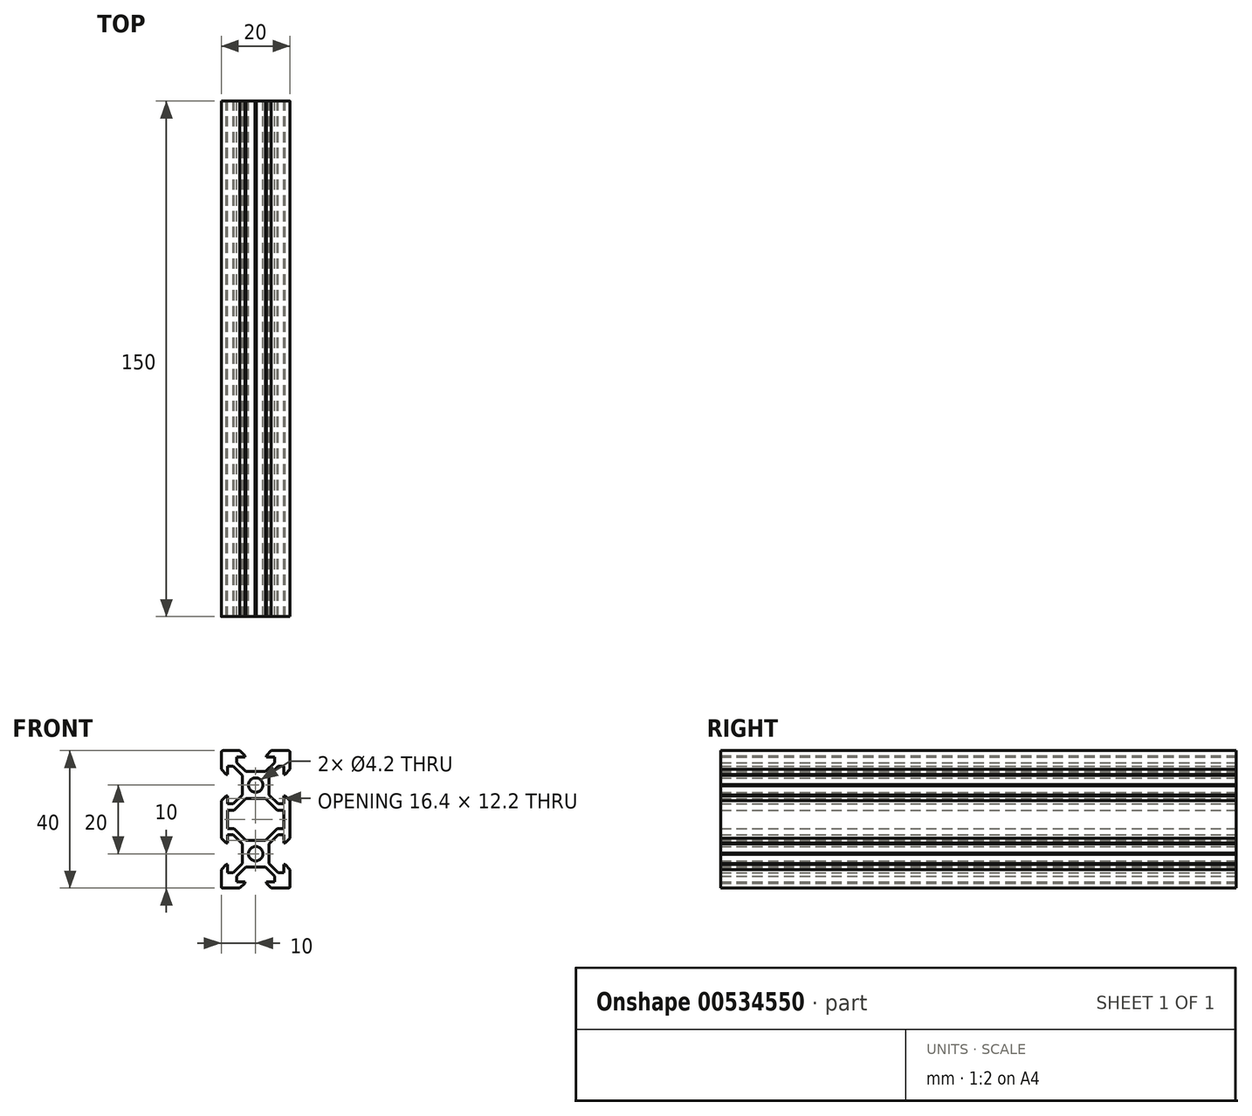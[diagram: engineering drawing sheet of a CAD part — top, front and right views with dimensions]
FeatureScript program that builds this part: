
annotation { "Feature Type Name" : "Feature", "Feature Type Description" : "" }
export const myFeature = defineFeature(function(context is Context, id is Id, definition is map)
    precondition{}
    {
        {
            var Q0;
            Q0=qCreatedBy(makeId("Front.planeOp"),FACE);
            var sketch = newSketch(context, id + "F0", { "sketchPlane" : qUnion([Q0])});
            skLineSegment(sketch, "E0.0.0", {"start": v(-3.69, 10) * mm, "end": v(-3.9, 9.79) * mm});
            skLineSegment(sketch, "E0.0.1", {"start": v(-3.9, 9.8) * mm, "end": v(-3.9, 7.16) * mm});
            skLineSegment(sketch, "E0.0.2", {"start": v(-3.9, 7.16) * mm, "end": v(-6.56, 4.5) * mm});
            skLineSegment(sketch, "E0.0.3", {"start": v(-6.56, 4.5) * mm, "end": v(-8.2, 4.5) * mm});
            skLineSegment(sketch, "E0.0.4", {"start": v(-8.2, 4.5) * mm, "end": v(-8.2, 6.88) * mm});
            skLineSegment(sketch, "E0.0.5", {"start": v(-8.2, 6.87) * mm, "end": v(-8.54, 6.87) * mm});
            skLineSegment(sketch, "E0.0.6", {"start": v(-8.54, 6.87) * mm, "end": v(-10, 5.42) * mm});
            skLineSegment(sketch, "E0.0.7", {"start": v(-10, 5.42) * mm, "end": v(-10, -5.42) * mm});
            skLineSegment(sketch, "E0.0.8", {"start": v(-10, -5.42) * mm, "end": v(-8.54, -6.87) * mm});
            skLineSegment(sketch, "E0.0.9", {"start": v(-8.54, -6.88) * mm, "end": v(-8.2, -6.88) * mm});
            skLineSegment(sketch, "E0.0.10", {"start": v(-8.2, -6.87) * mm, "end": v(-8.2, -4.5) * mm});
            skLineSegment(sketch, "E0.0.11", {"start": v(-8.2, -4.5) * mm, "end": v(-6.56, -4.5) * mm});
            skLineSegment(sketch, "E0.0.12", {"start": v(-6.56, -4.5) * mm, "end": v(-3.9, -7.16) * mm});
            skLineSegment(sketch, "E0.0.13", {"start": v(-3.9, -7.16) * mm, "end": v(-3.9, -9.79) * mm});
            skLineSegment(sketch, "E0.0.14", {"start": v(-3.9, -9.79) * mm, "end": v(-3.69, -10) * mm});
            skLineSegment(sketch, "E0.0.15", {"start": v(-3.69, -10) * mm, "end": v(-3.9, -10.21) * mm});
            skLineSegment(sketch, "E0.0.16", {"start": v(-3.9, -10.2) * mm, "end": v(-3.9, -12.84) * mm});
            skLineSegment(sketch, "E0.0.17", {"start": v(-3.9, -12.84) * mm, "end": v(-6.56, -15.5) * mm});
            skLineSegment(sketch, "E0.0.18", {"start": v(-6.56, -15.5) * mm, "end": v(-8.2, -15.5) * mm});
            skLineSegment(sketch, "E0.0.19", {"start": v(-8.2, -15.5) * mm, "end": v(-8.2, -13.12) * mm});
            skLineSegment(sketch, "E0.0.20", {"start": v(-8.2, -13.13) * mm, "end": v(-8.54, -13.13) * mm});
            skLineSegment(sketch, "E0.0.21", {"start": v(-8.54, -13.12) * mm, "end": v(-10, -14.58) * mm});
            skLineSegment(sketch, "E0.0.22", {"start": v(-10, -14.58) * mm, "end": v(-10, -19.5) * mm});
            skArc(sketch, "E0.0.23", {"start": v(-10, -19.5) * mm, "mid": v(-9.85, -19.85) * mm, "end": v(-9.5, -20) * mm});
            skLineSegment(sketch, "E0.0.24", {"start": v(-9.5, -20) * mm, "end": v(-4.58, -20) * mm});
            skLineSegment(sketch, "E0.0.25", {"start": v(-4.58, -20) * mm, "end": v(-3.13, -18.55) * mm});
            skLineSegment(sketch, "E0.0.26", {"start": v(-3.13, -18.54) * mm, "end": v(-3.13, -18.2) * mm});
            skLineSegment(sketch, "E0.0.27", {"start": v(-3.13, -18.2) * mm, "end": v(-5.5, -18.2) * mm});
            skLineSegment(sketch, "E0.0.28", {"start": v(-5.5, -18.2) * mm, "end": v(-5.5, -16.56) * mm});
            skLineSegment(sketch, "E0.0.29", {"start": v(-5.5, -16.56) * mm, "end": v(-2.84, -13.9) * mm});
            skLineSegment(sketch, "E0.0.30", {"start": v(-2.84, -13.9) * mm, "end": v(-0.21, -13.9) * mm});
            skLineSegment(sketch, "E0.0.31", {"start": v(-0.21, -13.9) * mm, "end": v(0, -13.7) * mm});
            skLineSegment(sketch, "E0.0.32", {"start": v(0, -13.69) * mm, "end": v(0.2, -13.9) * mm});
            skLineSegment(sketch, "E0.0.33", {"start": v(0.2, -13.9) * mm, "end": v(2.84, -13.9) * mm});
            skLineSegment(sketch, "E0.0.34", {"start": v(2.84, -13.9) * mm, "end": v(5.5, -16.56) * mm});
            skLineSegment(sketch, "E0.0.35", {"start": v(5.5, -16.56) * mm, "end": v(5.5, -18.2) * mm});
            skLineSegment(sketch, "E0.0.36", {"start": v(5.5, -18.2) * mm, "end": v(3.12, -18.2) * mm});
            skLineSegment(sketch, "E0.0.37", {"start": v(3.12, -18.2) * mm, "end": v(3.12, -18.54) * mm});
            skLineSegment(sketch, "E0.0.38", {"start": v(3.12, -18.54) * mm, "end": v(4.58, -20) * mm});
            skLineSegment(sketch, "E0.0.39", {"start": v(4.58, -20) * mm, "end": v(9.5, -20) * mm});
            skArc(sketch, "E0.0.40", {"start": v(9.5, -20) * mm, "mid": v(9.85, -19.85) * mm, "end": v(10, -19.5) * mm});
            skLineSegment(sketch, "E0.0.41", {"start": v(10, -19.5) * mm, "end": v(10, -14.58) * mm});
            skLineSegment(sketch, "E0.0.42", {"start": v(10, -14.58) * mm, "end": v(8.54, -13.12) * mm});
            skLineSegment(sketch, "E0.0.43", {"start": v(8.55, -13.13) * mm, "end": v(8.2, -13.13) * mm});
            skLineSegment(sketch, "E0.0.44", {"start": v(8.2, -13.12) * mm, "end": v(8.2, -15.5) * mm});
            skLineSegment(sketch, "E0.0.45", {"start": v(8.2, -15.5) * mm, "end": v(6.56, -15.5) * mm});
            skLineSegment(sketch, "E0.0.46", {"start": v(6.56, -15.5) * mm, "end": v(3.9, -12.84) * mm});
            skLineSegment(sketch, "E0.0.47", {"start": v(3.9, -12.84) * mm, "end": v(3.9, -10.2) * mm});
            skLineSegment(sketch, "E0.0.48", {"start": v(3.9, -10.21) * mm, "end": v(3.69, -10) * mm});
            skLineSegment(sketch, "E0.0.49", {"start": v(3.7, -10) * mm, "end": v(3.9, -9.79) * mm});
            skLineSegment(sketch, "E0.0.50", {"start": v(3.9, -9.79) * mm, "end": v(3.9, -7.16) * mm});
            skLineSegment(sketch, "E0.0.51", {"start": v(3.9, -7.16) * mm, "end": v(6.56, -4.5) * mm});
            skLineSegment(sketch, "E0.0.52", {"start": v(6.56, -4.5) * mm, "end": v(8.2, -4.5) * mm});
            skLineSegment(sketch, "E0.0.53", {"start": v(8.2, -4.5) * mm, "end": v(8.2, -6.87) * mm});
            skLineSegment(sketch, "E0.0.54", {"start": v(8.2, -6.88) * mm, "end": v(8.55, -6.88) * mm});
            skLineSegment(sketch, "E0.0.55", {"start": v(8.55, -6.87) * mm, "end": v(10, -5.42) * mm});
            skLineSegment(sketch, "E0.0.56", {"start": v(10, -5.42) * mm, "end": v(10, 5.42) * mm});
            skLineSegment(sketch, "E0.0.57", {"start": v(10, 5.42) * mm, "end": v(8.55, 6.87) * mm});
            skLineSegment(sketch, "E0.0.58", {"start": v(8.55, 6.87) * mm, "end": v(8.2, 6.87) * mm});
            skLineSegment(sketch, "E0.0.59", {"start": v(8.2, 6.88) * mm, "end": v(8.2, 4.5) * mm});
            skLineSegment(sketch, "E0.0.60", {"start": v(8.2, 4.5) * mm, "end": v(6.56, 4.5) * mm});
            skLineSegment(sketch, "E0.0.61", {"start": v(6.56, 4.5) * mm, "end": v(3.9, 7.16) * mm});
            skLineSegment(sketch, "E0.0.62", {"start": v(3.9, 7.16) * mm, "end": v(3.9, 9.8) * mm});
            skLineSegment(sketch, "E0.0.63", {"start": v(3.9, 9.79) * mm, "end": v(3.69, 10) * mm});
            skLineSegment(sketch, "E0.0.64", {"start": v(3.7, 10) * mm, "end": v(3.9, 10.2) * mm});
            skLineSegment(sketch, "E0.0.65", {"start": v(3.9, 10.21) * mm, "end": v(3.9, 12.84) * mm});
            skLineSegment(sketch, "E0.0.66", {"start": v(3.9, 12.84) * mm, "end": v(6.56, 15.5) * mm});
            skLineSegment(sketch, "E0.0.67", {"start": v(6.56, 15.5) * mm, "end": v(8.2, 15.5) * mm});
            skLineSegment(sketch, "E0.0.68", {"start": v(8.2, 15.5) * mm, "end": v(8.2, 13.13) * mm});
            skLineSegment(sketch, "E0.0.69", {"start": v(8.2, 13.12) * mm, "end": v(8.55, 13.12) * mm});
            skLineSegment(sketch, "E0.0.70", {"start": v(8.55, 13.12) * mm, "end": v(10, 14.58) * mm});
            skLineSegment(sketch, "E0.0.71", {"start": v(10, 14.58) * mm, "end": v(10, 19.5) * mm});
            skArc(sketch, "E0.0.72", {"start": v(10, 19.5) * mm, "mid": v(9.85, 19.85) * mm, "end": v(9.5, 20) * mm});
            skLineSegment(sketch, "E0.0.73", {"start": v(9.5, 20) * mm, "end": v(4.58, 20) * mm});
            skLineSegment(sketch, "E0.0.74", {"start": v(4.58, 20) * mm, "end": v(3.13, 18.55) * mm});
            skLineSegment(sketch, "E0.0.75", {"start": v(3.13, 18.55) * mm, "end": v(3.13, 18.2) * mm});
            skLineSegment(sketch, "E0.0.76", {"start": v(3.13, 18.2) * mm, "end": v(5.5, 18.2) * mm});
            skLineSegment(sketch, "E0.0.77", {"start": v(5.5, 18.2) * mm, "end": v(5.5, 16.56) * mm});
            skLineSegment(sketch, "E0.0.78", {"start": v(5.5, 16.56) * mm, "end": v(2.84, 13.9) * mm});
            skLineSegment(sketch, "E0.0.79", {"start": v(2.84, 13.9) * mm, "end": v(0.21, 13.9) * mm});
            skLineSegment(sketch, "E0.0.80", {"start": v(0.21, 13.9) * mm, "end": v(0, 13.7) * mm});
            skLineSegment(sketch, "E0.0.81", {"start": v(0, 13.7) * mm, "end": v(-0.21, 13.9) * mm});
            skLineSegment(sketch, "E0.0.82", {"start": v(-0.2, 13.9) * mm, "end": v(-2.84, 13.9) * mm});
            skLineSegment(sketch, "E0.0.83", {"start": v(-2.84, 13.9) * mm, "end": v(-5.5, 16.56) * mm});
            skLineSegment(sketch, "E0.0.84", {"start": v(-5.5, 16.56) * mm, "end": v(-5.5, 18.2) * mm});
            skLineSegment(sketch, "E0.0.85", {"start": v(-5.5, 18.2) * mm, "end": v(-3.12, 18.2) * mm});
            skLineSegment(sketch, "E0.0.86", {"start": v(-3.12, 18.2) * mm, "end": v(-3.12, 18.55) * mm});
            skLineSegment(sketch, "E0.0.87", {"start": v(-3.12, 18.55) * mm, "end": v(-4.58, 20) * mm});
            skLineSegment(sketch, "E0.0.88", {"start": v(-4.58, 20) * mm, "end": v(-9.5, 20) * mm});
            skArc(sketch, "E0.0.89", {"start": v(-9.5, 20) * mm, "mid": v(-9.85, 19.85) * mm, "end": v(-10, 19.5) * mm});
            skLineSegment(sketch, "E0.0.90", {"start": v(-10, 19.5) * mm, "end": v(-10, 14.58) * mm});
            skLineSegment(sketch, "E0.0.91", {"start": v(-10, 14.58) * mm, "end": v(-8.55, 13.12) * mm});
            skLineSegment(sketch, "E0.0.92", {"start": v(-8.54, 13.12) * mm, "end": v(-8.2, 13.12) * mm});
            skLineSegment(sketch, "E0.0.93", {"start": v(-8.2, 13.13) * mm, "end": v(-8.2, 15.5) * mm});
            skLineSegment(sketch, "E0.0.94", {"start": v(-8.2, 15.5) * mm, "end": v(-6.56, 15.5) * mm});
            skLineSegment(sketch, "E0.0.95", {"start": v(-6.56, 15.5) * mm, "end": v(-3.9, 12.84) * mm});
            skLineSegment(sketch, "E0.0.96", {"start": v(-3.9, 12.84) * mm, "end": v(-3.9, 10.21) * mm});
            skLineSegment(sketch, "E0.0.97", {"start": v(-3.9, 10.2) * mm, "end": v(-3.7, 10) * mm});
            skCircle(sketch, "E1.0", {"center": v(0, 10) * mm, "radius": 2.1 * mm});
            skCircle(sketch, "E2.0", {"center": v(0, -10) * mm, "radius": 2.1 * mm});
            skLineSegment(sketch, "E3.0", {"start": v(-8.2, -2.7) * mm, "end": v(-8.2, 2.7) * mm});
            skLineSegment(sketch, "E4.0", {"start": v(-8.2, 2.7) * mm, "end": v(-6.24, 2.7) * mm});
            skLineSegment(sketch, "E5.0", {"start": v(-6.24, 2.7) * mm, "end": v(-2.84, 6.1) * mm});
            skLineSegment(sketch, "E6.0", {"start": v(2.84, 6.1) * mm, "end": v(-2.84, 6.1) * mm});
            skLineSegment(sketch, "E7.0", {"start": v(6.24, 2.7) * mm, "end": v(2.84, 6.1) * mm});
            skLineSegment(sketch, "E8.0", {"start": v(8.2, 2.7) * mm, "end": v(6.24, 2.7) * mm});
            skLineSegment(sketch, "E9.0", {"start": v(8.2, -2.7) * mm, "end": v(8.2, 2.7) * mm});
            skLineSegment(sketch, "E10.0", {"start": v(8.2, -2.7) * mm, "end": v(6.24, -2.7) * mm});
            skLineSegment(sketch, "E11.0", {"start": v(6.24, -2.7) * mm, "end": v(2.84, -6.1) * mm});
            skLineSegment(sketch, "E12.0", {"start": v(2.84, -6.1) * mm, "end": v(-2.84, -6.1) * mm});
            skLineSegment(sketch, "E13.0", {"start": v(-6.24, -2.7) * mm, "end": v(-2.84, -6.1) * mm});
            skPoint(sketch, "E14.0", {"position": v(-7.22, -2.7) * mm});
            skLineSegment(sketch, "E15", {"start": v(-8.2, -2.7) * mm, "end": v(-6.24, -2.7) * mm});
            skSolve(sketch);
        }
        {
            var Q0;
            Q0 = qSketchRegion(id + "F0", true);
            extrude(context, id + "F1", {"entities" : qUnion([Q0]), "depth" : 150 * mm, "offsetDistance" : 25 * mm});
        }
    });
